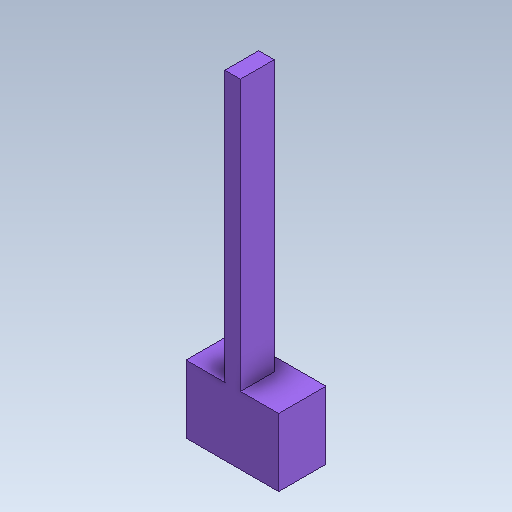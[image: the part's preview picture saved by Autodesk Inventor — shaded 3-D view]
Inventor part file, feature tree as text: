
AUTODESK INVENTOR PART (.ipt)
format: ipt  version: 2020 (Build 240168000, 168)  size: 122,880 bytes
history: native  units: in
note: dims shown in document units (in); Inventor stores cm internally (conversion verified against a paired STEP export)
features: sketch x13, other x3
ambient origin geometry x8: Origin, YZ Plane, XZ Plane, XY Plane, X Axis, Y Axis, Z Axis, Center Point
bodies: Solid1 (feature_tree)
feature tree (16):
  other  "PistonTop.ipt"
  other  "Solid1::PistonTop.ipt"
  other  "TaggingFeature1"
  sketch  "Sketch1"  dims[d0=0.3937in]
  sketch  "Sketch4"
  sketch  "Sketch5"
  sketch  "Sketch6"
  sketch  "Sketch7"
  sketch  "Sketch8"
  sketch  "Sketch9"
  sketch  "Sketch10"
  sketch  "Sketch11"
  sketch  "Sketch12"
  sketch  "Sketch17"
  sketch  "Sketch18"
  sketch  "Sketch19"
